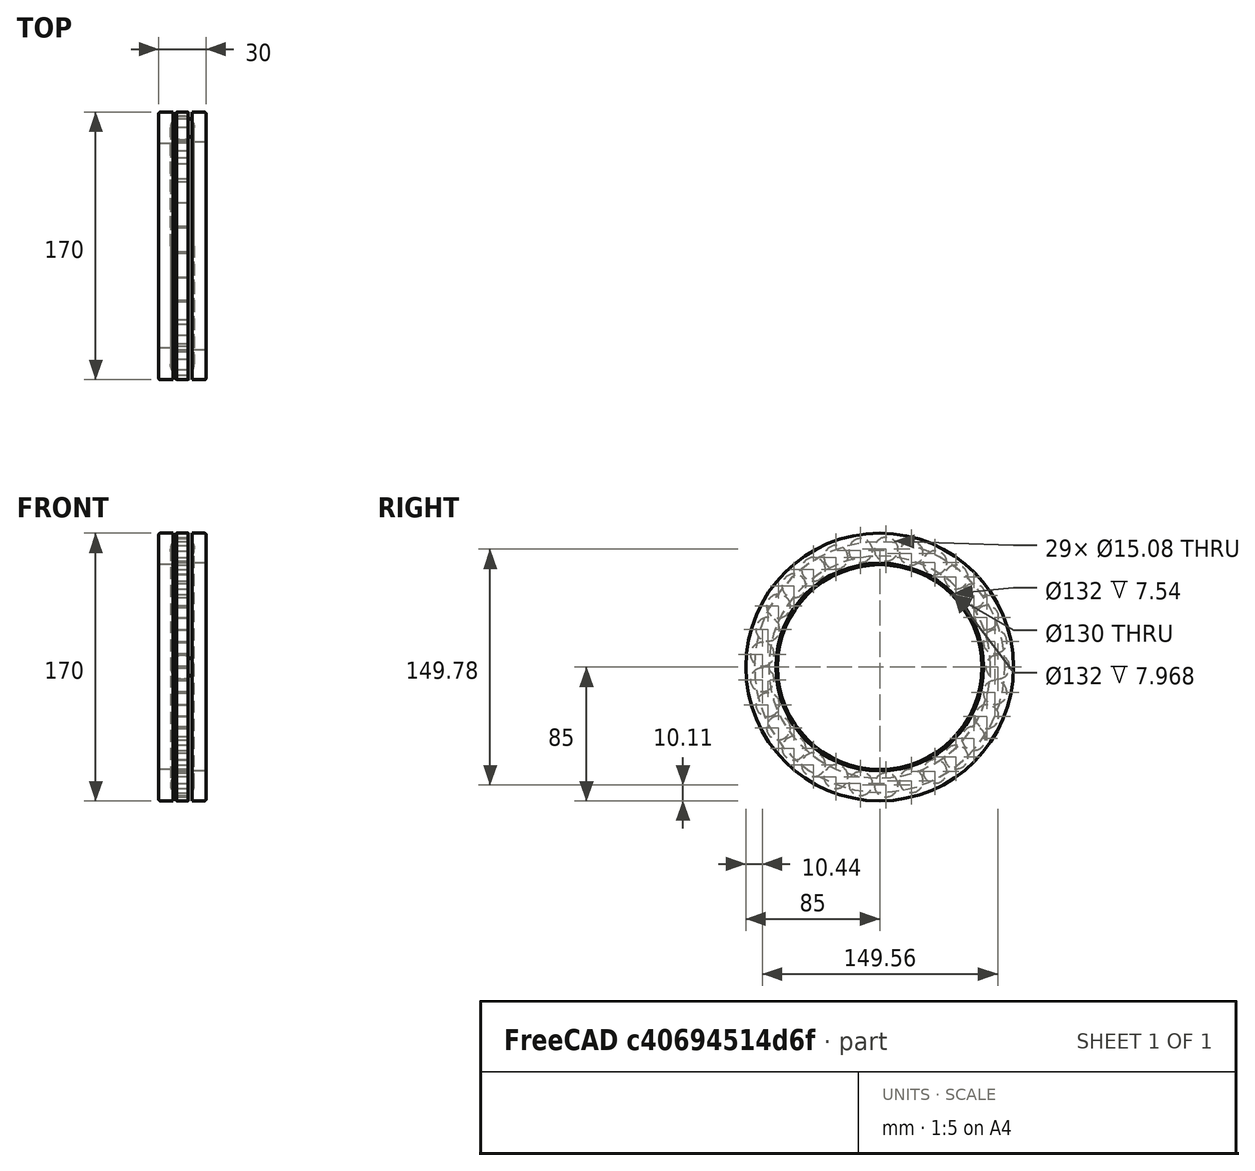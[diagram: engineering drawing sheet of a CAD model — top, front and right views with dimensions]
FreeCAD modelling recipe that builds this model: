
FCSTD DOCUMENT  (FreeCAD 2020.10.16R22739 +2665 (Git))
Label: lozysko 51126
License: All rights reserved
LicenseURL: http://en.wikipedia.org/wiki/All_rights_reserved
objects: App::Link×28, Part::Feature×4, Part::FeaturePython×3, App::FeaturePython×2
note: 6 computed .brp shape members not serialized (recipe doc carries the construction recipe); baked Part::Feature solids carry a one-line shape summary decoded from their .brp

FEATURE [Part::Feature] Solid  label="_51126_PART1"
  shape: bbox 7.541 x 184 x 184 mm, 35 faces (baked)
FEATURE [Part::Feature] Solid001  label="_51126_PART2"
  shape: bbox 9.646 x 184 x 184 mm, 9 faces (baked)
FEATURE [Part::Feature] Solid002  label="_51126_PART3"
  shape: bbox 15 x 184 x 184 mm, 8 faces (baked)
FEATURE [Part::Feature] Solid003  label="_51126_PART4"
  shape: bbox 15.08 x 15.08 x 15.08 mm, 1 faces (baked)
FEATURE [App::Link] Link  label="_51126_PART005"
  LinkPlacement = pos=(0,0,0) rot=(-1,0,0;0.216662rad)
  LinkedObject = -> Solid003
  Placement = pos=(0,0,0) rot=(-1,0,0;0.216662rad)
  SyncGroupVisibility = false
  _LinkVersion = 1
FEATURE [App::Link] Link001  label="_51126_PART006"
  LinkPlacement = pos=(0,0,0) rot=(-1,0,0;0.433323rad)
  LinkedObject = -> Solid003
  Placement = pos=(0,0,0) rot=(-1,0,0;0.433323rad)
  SyncGroupVisibility = false
  _LinkVersion = 1
FEATURE [App::Link] Link002  label="_51126_PART007"
  LinkPlacement = pos=(0,0,0) rot=(-1,0,0;0.649985rad)
  LinkedObject = -> Solid003
  Placement = pos=(0,0,0) rot=(-1,0,0;0.649985rad)
  SyncGroupVisibility = false
  _LinkVersion = 1
FEATURE [App::Link] Link003  label="_51126_PART008"
  LinkPlacement = pos=(0,0,0) rot=(-1,0,0;0.866646rad)
  LinkedObject = -> Solid003
  Placement = pos=(0,0,0) rot=(-1,0,0;0.866646rad)
  SyncGroupVisibility = false
  _LinkVersion = 1
FEATURE [App::Link] Link004  label="_51126_PART009"
  LinkPlacement = pos=(0,0,0) rot=(-1,0,0;1.08331rad)
  LinkedObject = -> Solid003
  Placement = pos=(0,0,0) rot=(-1,0,0;1.08331rad)
  SyncGroupVisibility = false
  _LinkVersion = 1
FEATURE [App::Link] Link005  label="_51126_PART010"
  LinkPlacement = pos=(0,0,0) rot=(-1,0,0;1.29997rad)
  LinkedObject = -> Solid003
  Placement = pos=(0,0,0) rot=(-1,0,0;1.29997rad)
  SyncGroupVisibility = false
  _LinkVersion = 1
FEATURE [App::Link] Link006  label="_51126_PART011"
  LinkPlacement = pos=(0,0,0) rot=(-1,0,0;1.51663rad)
  LinkedObject = -> Solid003
  Placement = pos=(0,0,0) rot=(-1,0,0;1.51663rad)
  SyncGroupVisibility = false
  _LinkVersion = 1
FEATURE [App::Link] Link007  label="_51126_PART012"
  LinkPlacement = pos=(0,0,0) rot=(-1,0,0;1.73329rad)
  LinkedObject = -> Solid003
  Placement = pos=(0,0,0) rot=(-1,0,0;1.73329rad)
  SyncGroupVisibility = false
  _LinkVersion = 1
FEATURE [App::Link] Link008  label="_51126_PART013"
  LinkPlacement = pos=(0,0,0) rot=(-1,0,0;1.94995rad)
  LinkedObject = -> Solid003
  Placement = pos=(0,0,0) rot=(-1,0,0;1.94995rad)
  SyncGroupVisibility = false
  _LinkVersion = 1
FEATURE [App::Link] Link009  label="_51126_PART014"
  LinkPlacement = pos=(0,0,0) rot=(1,0,0;4.11657rad)
  LinkedObject = -> Solid003
  Placement = pos=(0,0,0) rot=(1,0,0;4.11657rad)
  SyncGroupVisibility = false
  _LinkVersion = 1
FEATURE [App::Link] Link010  label="_51126_PART015"
  LinkPlacement = pos=(0,0,0) rot=(1,0,0;3.89991rad)
  LinkedObject = -> Solid003
  Placement = pos=(0,0,0) rot=(1,0,0;3.89991rad)
  SyncGroupVisibility = false
  _LinkVersion = 1
FEATURE [App::Link] Link011  label="_51126_PART016"
  LinkPlacement = pos=(0,0,0) rot=(1,0,0;3.68325rad)
  LinkedObject = -> Solid003
  Placement = pos=(0,0,0) rot=(1,0,0;3.68325rad)
  SyncGroupVisibility = false
  _LinkVersion = 1
FEATURE [App::Link] Link012  label="_51126_PART017"
  LinkPlacement = pos=(0,0,0) rot=(1,0,0;3.46658rad)
  LinkedObject = -> Solid003
  Placement = pos=(0,0,0) rot=(1,0,0;3.46658rad)
  SyncGroupVisibility = false
  _LinkVersion = 1
FEATURE [App::Link] Link013  label="_51126_PART018"
  LinkPlacement = pos=(0,0,0) rot=(1,0,0;3.24992rad)
  LinkedObject = -> Solid003
  Placement = pos=(0,0,0) rot=(1,0,0;3.24992rad)
  SyncGroupVisibility = false
  _LinkVersion = 1
FEATURE [App::Link] Link014  label="_51126_PART019"
  LinkPlacement = pos=(0,0,0) rot=(1,0,0;3.03326rad)
  LinkedObject = -> Solid003
  Placement = pos=(0,0,0) rot=(1,0,0;3.03326rad)
  SyncGroupVisibility = false
  _LinkVersion = 1
FEATURE [App::Link] Link015  label="_51126_PART020"
  LinkPlacement = pos=(0,0,0) rot=(1,0,0;2.8166rad)
  LinkedObject = -> Solid003
  Placement = pos=(0,0,0) rot=(1,0,0;2.8166rad)
  SyncGroupVisibility = false
  _LinkVersion = 1
FEATURE [App::Link] Link016  label="_51126_PART021"
  LinkPlacement = pos=(0,0,0) rot=(1,0,0;2.59994rad)
  LinkedObject = -> Solid003
  Placement = pos=(0,0,0) rot=(1,0,0;2.59994rad)
  SyncGroupVisibility = false
  _LinkVersion = 1
FEATURE [App::Link] Link017  label="_51126_PART022"
  LinkPlacement = pos=(0,0,0) rot=(1,0,0;2.38328rad)
  LinkedObject = -> Solid003
  Placement = pos=(0,0,0) rot=(1,0,0;2.38328rad)
  SyncGroupVisibility = false
  _LinkVersion = 1
FEATURE [App::Link] Link018  label="_51126_PART023"
  LinkPlacement = pos=(0,0,0) rot=(1,0,0;2.16662rad)
  LinkedObject = -> Solid003
  Placement = pos=(0,0,0) rot=(1,0,0;2.16662rad)
  SyncGroupVisibility = false
  _LinkVersion = 1
FEATURE [App::Link] Link019  label="_51126_PART024"
  LinkPlacement = pos=(0,0,0) rot=(1,0,0;1.94995rad)
  LinkedObject = -> Solid003
  Placement = pos=(0,0,0) rot=(1,0,0;1.94995rad)
  SyncGroupVisibility = false
  _LinkVersion = 1
FEATURE [App::Link] Link020  label="_51126_PART025"
  LinkPlacement = pos=(0,0,0) rot=(1,0,0;1.73329rad)
  LinkedObject = -> Solid003
  Placement = pos=(0,0,0) rot=(1,0,0;1.73329rad)
  SyncGroupVisibility = false
  _LinkVersion = 1
FEATURE [App::Link] Link021  label="_51126_PART026"
  LinkPlacement = pos=(0,0,0) rot=(1,0,0;1.51663rad)
  LinkedObject = -> Solid003
  Placement = pos=(0,0,0) rot=(1,0,0;1.51663rad)
  SyncGroupVisibility = false
  _LinkVersion = 1
FEATURE [App::Link] Link022  label="_51126_PART027"
  LinkPlacement = pos=(0,0,0) rot=(1,0,0;1.29997rad)
  LinkedObject = -> Solid003
  Placement = pos=(0,0,0) rot=(1,0,0;1.29997rad)
  SyncGroupVisibility = false
  _LinkVersion = 1
FEATURE [App::Link] Link023  label="_51126_PART028"
  LinkPlacement = pos=(0,0,0) rot=(1,0,0;1.08331rad)
  LinkedObject = -> Solid003
  Placement = pos=(0,0,0) rot=(1,0,0;1.08331rad)
  SyncGroupVisibility = false
  _LinkVersion = 1
FEATURE [App::Link] Link024  label="_51126_PART029"
  LinkPlacement = pos=(0,0,0) rot=(1,0,0;0.866646rad)
  LinkedObject = -> Solid003
  Placement = pos=(0,0,0) rot=(1,0,0;0.866646rad)
  SyncGroupVisibility = false
  _LinkVersion = 1
FEATURE [App::Link] Link025  label="_51126_PART030"
  LinkPlacement = pos=(0,0,0) rot=(1,0,0;0.649985rad)
  LinkedObject = -> Solid003
  Placement = pos=(0,0,0) rot=(1,0,0;0.649985rad)
  SyncGroupVisibility = false
  _LinkVersion = 1
FEATURE [App::Link] Link026  label="_51126_PART031"
  LinkPlacement = pos=(0,0,0) rot=(1,0,0;0.433323rad)
  LinkedObject = -> Solid003
  Placement = pos=(0,0,0) rot=(1,0,0;0.433323rad)
  SyncGroupVisibility = false
  _LinkVersion = 1
FEATURE [App::Link] Link027  label="_51126_PART032"
  LinkPlacement = pos=(0,0,0) rot=(1,0,0;0.216662rad)
  LinkedObject = -> Solid003
  Placement = pos=(0,0,0) rot=(1,0,0;0.216662rad)
  SyncGroupVisibility = false
  _LinkVersion = 1
FEATURE [App::FeaturePython] Constraints  # WARN: FeaturePython — macro-defined, semantics opaque (R4)
  _LinkVersion = 1
  _Version = 1
FEATURE [Part::FeaturePython] Parts  # WARN: FeaturePython — macro-defined, semantics opaque (R4)
  Group = -> [Solid,Solid001,Solid002,Solid003,Link,Link001,Link002,Link003,Link004,Link005,Link006,Link007,Link008,Link009,Link010,Link011,Link012,Link013,Link014,Link015,Link016,Link017,Link018,Link019,Link020,Link021,Link022,Link023,Link024,Link025,Link026,Link027]
  GroupMode = 0
  _LinkVersion = 1
FEATURE [Part::FeaturePython] Assembly  label="51126-lozysko"  # WARN: FeaturePython — macro-defined, semantics opaque (R4)
  AutoRelax = true
  BuildShape = 0
  Freeze = false
  Group = -> [Constraints,Elements,Parts]
  Verbose = false
  _LinkVersion = 1
  _SolverType = 1
  _Version = 1
FEATURE [App::FeaturePython] Elements  # WARN: FeaturePython — macro-defined, semantics opaque (R4)
  Group = -> [Element]
  _LinkVersion = 1
FEATURE [Part::FeaturePython] Element  # link proxy (typed FeaturePython)
  Detach = false
  LinkTransform = true
  LinkedObject = -> Solid001 [Face1]
  _LinkVersion = 1
  _Parent = -> Elements
